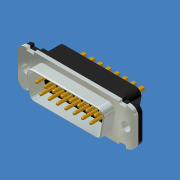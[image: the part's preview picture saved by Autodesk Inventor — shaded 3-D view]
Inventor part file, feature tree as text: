
AUTODESK INVENTOR PART (.ipt)
format: ipt  version: 2019 (Build 230136000, 136)  size: 442,368 bytes
history: native  units: mm (DEFAULTED — no unit token found)
features: extrude x12, pattern_linear x6, sketch x4, fillet x4, chamfer x1
ambient origin geometry x8: Origin, YZ Plane, XZ Plane, XY Plane, X Axis, Y Axis, Z Axis, Center Point
bodies: Solid1 (feature_tree)
feature tree (27):
  sketch  "Sketch1"  dims[d0=1.745329mm d6=0.381mm d7=2.418418mm d8=0.855895mm d9=2.418418mm]
  extrude  "Extrusion1"  Depth=0.381mm
  extrude  "Extrusion2"  Depth=1.314425mm
  fillet  "Fillet4"  Radius=1.397mm
  extrude  "Pin1"  Depth=5.08mm TaperAngle=0.0deg
  extrude  "Pin2"  Depth=5.08mm TaperAngle=0.0deg
  extrude  "Pin50"  Depth=10.8966mm
  fillet  "Fillet1"  Radius=2.794mm
  fillet  "Fillet2"  Radius=70.0mm
  fillet  "Fillet50"  Radius=2.794mm
  extrude  "Extrusion5"  Depth=1.909443mm
  extrude  "Extrusion6"  Depth=0.254mm
  sketch  "Sketch4"  dims[d24=5.08mm d25=0.0mm d26=5.08mm d27=0.0mm d28=80.0mm d30=2.794mm d31=70.0mm d33=2.794mm d34=1.909443mm d35=0.254mm d36=1.6002mm d37=0.0mm d38=5.08mm d39=0.0mm d44=0.4953mm d45=0.4953mm d46=1.016mm d52=2.8448mm d53=5.08mm d54=0.0mm d55=0.4953mm d56=5.08mm d57=0.0mm d58=0.2032mm d59=0.2032mm d60=80.0mm d62=2.794mm d63=0.381mm d67=5.1054mm d68=0.0mm d69=5.6388mm d70=0.0mm d71=5.6388mm d72=0.0mm d73=5.6388mm d74=0.0mm d75=80.0mm d77=2.794mm d78=70.0mm d80=2.794mm d81=80.0mm d83=2.794mm d86=1.909443mm d87=10.8966mm d88=27.7876mm d91=45.0deg]
  extrude  "ExtrudeSgr50"  Depth=1.6002mm TaperAngle=0.0deg
  chamfer  "Chamfer50"  Distance=5.08mm
  pattern_linear  "Pattern1"  Spacing1=0.4953mm  [1 undecoded]
  pattern_linear  "Pattern2"  Spacing1=0.4953mm  [1 undecoded]
  pattern_linear  "Pattern50"  Spacing1=1.016mm  [1 undecoded]
  extrude  "Female"  Depth=10.8966mm
  extrude  "Socket1"  Depth=5.08mm
  extrude  "Socket2"  TaperAngle=0.0deg  [1 undecoded]
  extrude  "Socket50"  Depth=0.4953mm
  pattern_linear  "Pattern5"  Spacing1=5.08mm  [1 undecoded]
  pattern_linear  "Pattern6"  Spacing1=0.0mm  [1 undecoded]
  pattern_linear  "Pattern7"  Spacing1=0.2032mm  [1 undecoded]
  sketch  "Sketch2"  dims[d11=1.314425mm d15=2.54mm d19=1.397mm]
  sketch  "Sketch3"  dims[d20=1.27mm d21=0.0mm d22=5.08mm d23=0.0mm]
note: 7 required parameter values undecoded (feature->parameter linkage not recoverable at this tier; creation-order binding heuristic only, values carry confidence <= 0.55)
